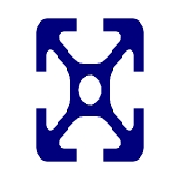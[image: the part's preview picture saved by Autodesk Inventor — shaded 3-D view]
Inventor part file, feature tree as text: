
AUTODESK INVENTOR PART (.ipt)
format: ipt  version: 2020 (Build 240168000, 168)  size: 273,408 bytes
history: native  units: mm
features: other x16, sketch x8
ambient origin geometry x8: Origin, YZ Plane, XZ Plane, XY Plane, X Axis, Y Axis, Z Axis, Center Point
bodies: Body (feature_tree)
feature tree (24):
  other  "Řízená délka"
  other  "Těleso1"
  other  "Start Plane"
  other  "End Plane"
  other  "iFeatureSketch"
  other  "DRAZKA_20:1"
  other  "DRAZKA_20:2"
  other  "DRAZKA_20:3"
  other  "DRAZKA_20:4"
  other  "DIRA_20:1"
  other  "DRAZKA_20:1Axis"
  other  "DRAZKA_20:2Axis"
  other  "DRAZKA_20:3Axis"
  other  "DRAZKA_20:4Axis"
  other  "DIRA_20:1Axis"
  sketch  "Sketch"  dims[d2=20.0mm d3=20.0mm d4=2.0mm d9=-0.0mm d10=150.8125mm d11=0.13mm d12=0.0mm d15=0.83mm d16=0.83mm d17=9.8mm d18=3.0mm d19=4.55mm d20=45.0deg d21=5.2mm d22=1.8mm d24=1.0mm d26=0.83mm d27=0.83mm d28=9.8mm d29=3.0mm d30=4.55mm d31=45.0deg d32=5.2mm d33=1.8mm d35=1.0mm d37=0.83mm d38=0.83mm d39=9.8mm d40=3.0mm d41=4.55mm d42=45.0deg d43=5.2mm d44=1.8mm d46=1.0mm d48=0.83mm d49=0.83mm d50=9.8mm d51=3.0mm d52=4.55mm d53=45.0deg d54=5.2mm d55=1.8mm d57=1.0mm d59=4.3mm d60=0.0mm d61=0.0mm d62=0.0mm d63=0.0mm d64=0.0mm d65=0.0mm d66=0.0mm d67=0.0mm d76=90.0deg d14=150.8125mm]
  sketch  "Náčrt11"
  other  "Pracovní rovina4"
  sketch  "Náčrt12"
  sketch  "Náčrt6"
  sketch  "Náčrt7"
  sketch  "Náčrt8"
  sketch  "Náčrt9"
  sketch  "Náčrt10"
